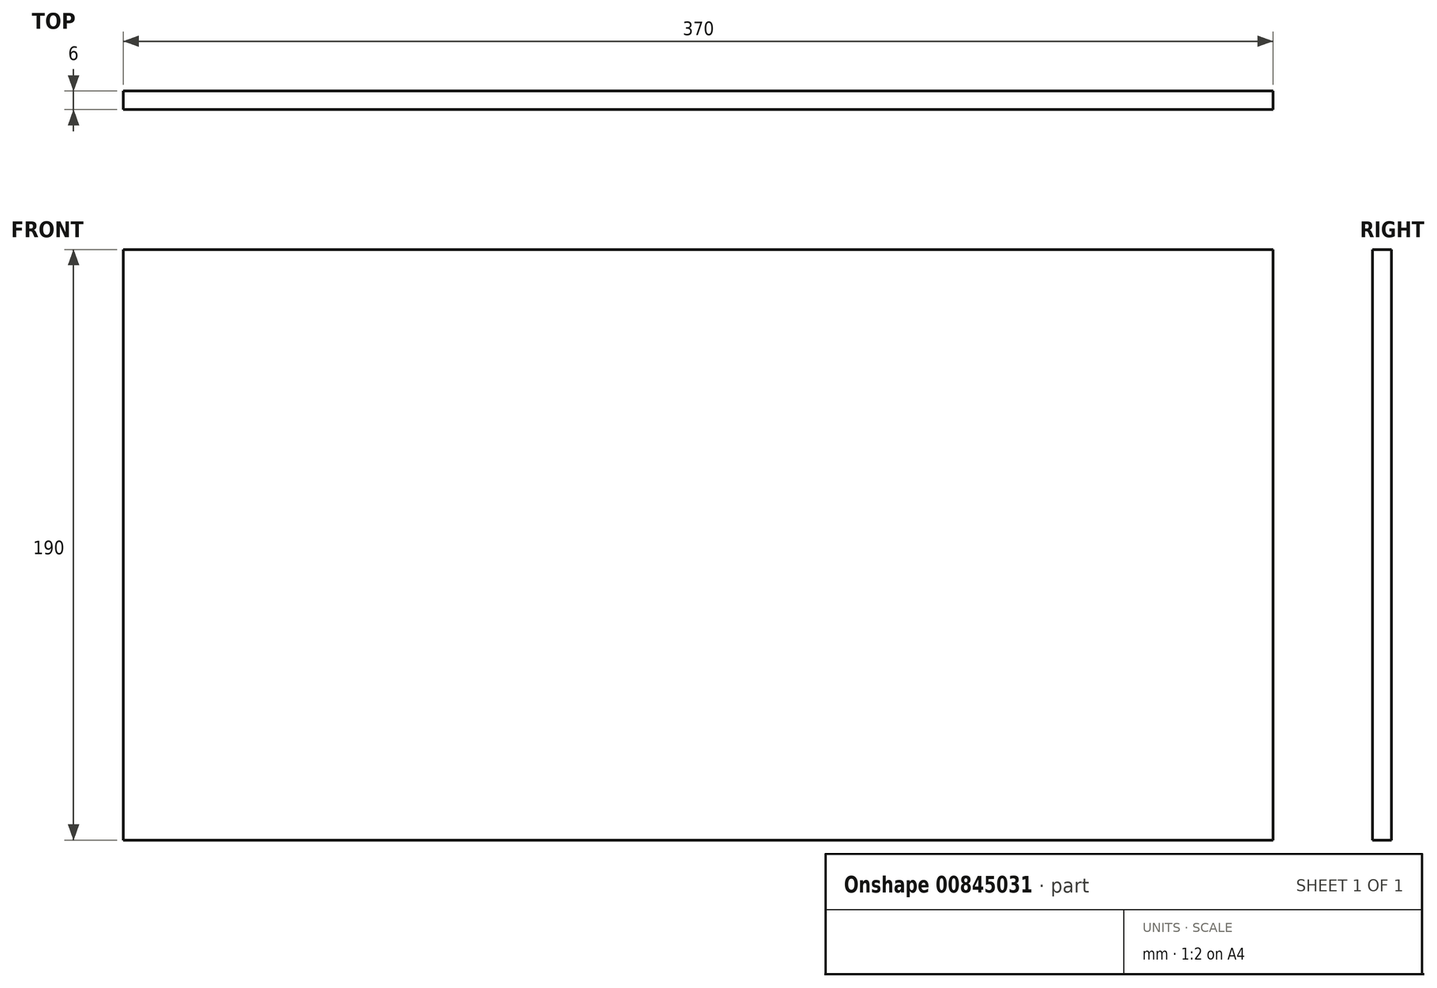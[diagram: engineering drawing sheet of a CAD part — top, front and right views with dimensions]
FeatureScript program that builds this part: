
annotation { "Feature Type Name" : "Feature", "Feature Type Description" : "" }
export const myFeature = defineFeature(function(context is Context, id is Id, definition is map)
    precondition{}
    {
        {
            var Q0;
            Q0=qCreatedBy(makeId("Front.planeOp"),FACE);
            var sketch = newSketch(context, id + "F0", { "sketchPlane" : qUnion([Q0])});
            skLineSegment(sketch, "E0.bottom", {"start": v(-185, 95) * mm, "end": v(185, 95) * mm});
            skLineSegment(sketch, "E0.top", {"start": v(-185, -95) * mm, "end": v(185, -95) * mm});
            skLineSegment(sketch, "E0.left", {"start": v(-185, 95) * mm, "end": v(-185, -95) * mm});
            skLineSegment(sketch, "E0.right", {"start": v(185, 95) * mm, "end": v(185, -95) * mm});
            skPoint(sketch, "E0.middle", {"position": v(0, 0) * mm});
            skSolve(sketch);
        }
        {
            var Q0;
            Q0=makeQuery(id+"F0.imprint","IMPRINT",FACE,{"disambiguationData":[TD([[makeQuery(id+"F0.imprint","IMPRINT",EDGE,{"derivedFrom":sQuery(id+"F0.wireOp",EDGE,"E0.bottom")}),-1.0]])]});
            extrude(context, id + "F1", {"entities" : qUnion([Q0]), "depth" : 6 * mm, "offsetDistance" : 25 * mm});
        }
    });
